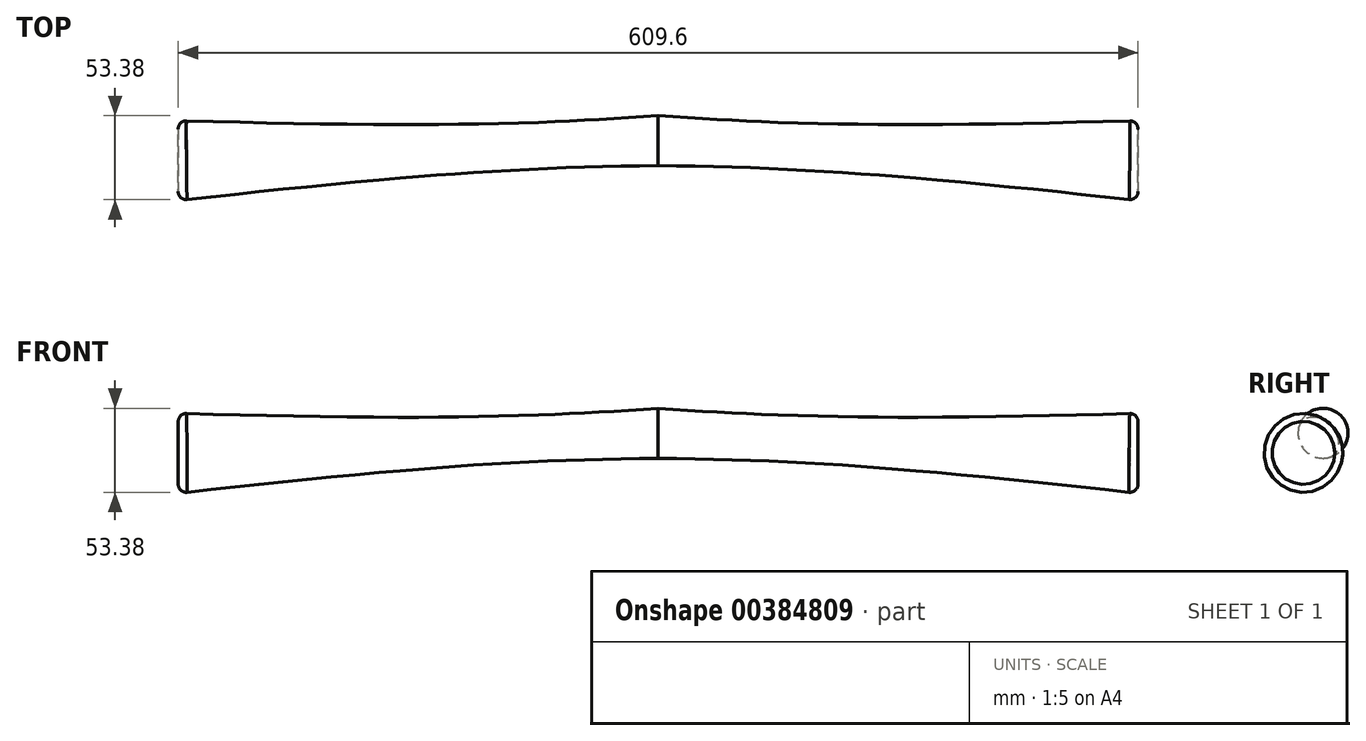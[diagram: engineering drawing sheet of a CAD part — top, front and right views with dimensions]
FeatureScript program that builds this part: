
annotation { "Feature Type Name" : "Feature", "Feature Type Description" : "" }
export const myFeature = defineFeature(function(context is Context, id is Id, definition is map)
    precondition{}
    {
        {
            var Q0;
            Q0=qCreatedBy(makeId("Right.planeOp"),FACE);
            cPlane(context, id + "F0", {"entities" : qUnion([Q0]), "cplaneType" : CPlaneType.OFFSET, "offset" : 304.8 * mm, "width" : 152.4 * mm, "height" : 152.4 * mm});
        }
        {
            var Q0;
            Q0=qCreatedBy(makeId("Right.planeOp"),FACE);
            var sketch = newSketch(context, id + "F1", { "sketchPlane" : qUnion([Q0])});
            skCircle(sketch, "E0", {"center": v(0, 0) * mm, "radius": 15.88 * mm});
            skSolve(sketch);
        }
        {
            var Q0;
            Q0=qCreatedBy(id+"F0.planeOp",FACE);
            var sketch = newSketch(context, id + "F2", { "sketchPlane" : qUnion([Q0])});
            skPoint(sketch, "E1", {"position": v(0, -12.7) * mm});
            skPoint(sketch, "E2", {"position": v(-12.7, -12.7) * mm});
            skCircle(sketch, "E3", {"center": v(-12.7, -12.7) * mm, "radius": 25.4 * mm});
            skSolve(sketch);
        }
        {
            var Q0;
            Q0=makeQuery(id+"F1.imprint","IMPRINT",FACE,{"disambiguationData":[TD([[makeQuery(id+"F1.imprint","IMPRINT",EDGE,{"derivedFrom":sQuery(id+"F1.wireOp",EDGE,"E0")}),1.0]])]});
            var Q1;
            Q1=makeQuery(id+"F2.imprint","IMPRINT",FACE,{"disambiguationData":[TD([[makeQuery(id+"F2.imprint","IMPRINT",EDGE,{"derivedFrom":sQuery(id+"F2.wireOp",EDGE,"E3")}),1.0]])]});
            loft(context, id + "F3", {"sheetProfilesArray" : [{ "sheetProfileEntities" : qUnion([Q0]) }, { "sheetProfileEntities" : qUnion([Q1]) }]});
        }
        {
            var Q0;
            Q0=makeQuery(id+"F3.opLoft","MID_CAP_EDGE",EDGE,{"disambiguationData":[OSD([sQuery(id+"F1.wireOp",EDGE,"E0"),sQuery(id+"F2.wireOp",EDGE,"E3")])],"capPos":1.0});
            fillet(context, id + "F4", {"entities" : qUnion([Q0]), "radius" : 5.08 * mm, "tangentPropagation" : true, "allowEdgeOverflow" : false});
        }
        {
            var Q0;
            Q0=makeQuery(id+"F3.opLoft","SWEPT_BODY",BODY,{"disambiguationData":[OSD([makeQuery(id+"F1.imprint","IMPRINT",FACE,{"disambiguationData":[TD([[makeQuery(id+"F1.imprint","IMPRINT",EDGE,{"derivedFrom":sQuery(id+"F1.wireOp",EDGE,"E0")}),1.0]])]}),makeQuery(id+"F2.imprint","IMPRINT",FACE,{"disambiguationData":[TD([[makeQuery(id+"F2.imprint","IMPRINT",EDGE,{"derivedFrom":sQuery(id+"F2.wireOp",EDGE,"E3")}),1.0]])]})])]});
            var Q1;
            Q1=qCreatedBy(makeId("Right.planeOp"),FACE);
            mirror(context, id + "F5", {"operationType" : NewBodyOperationType.ADD, "entities" : qUnion([Q0]), "mirrorPlane" : qUnion([Q1])});
        }
    });
